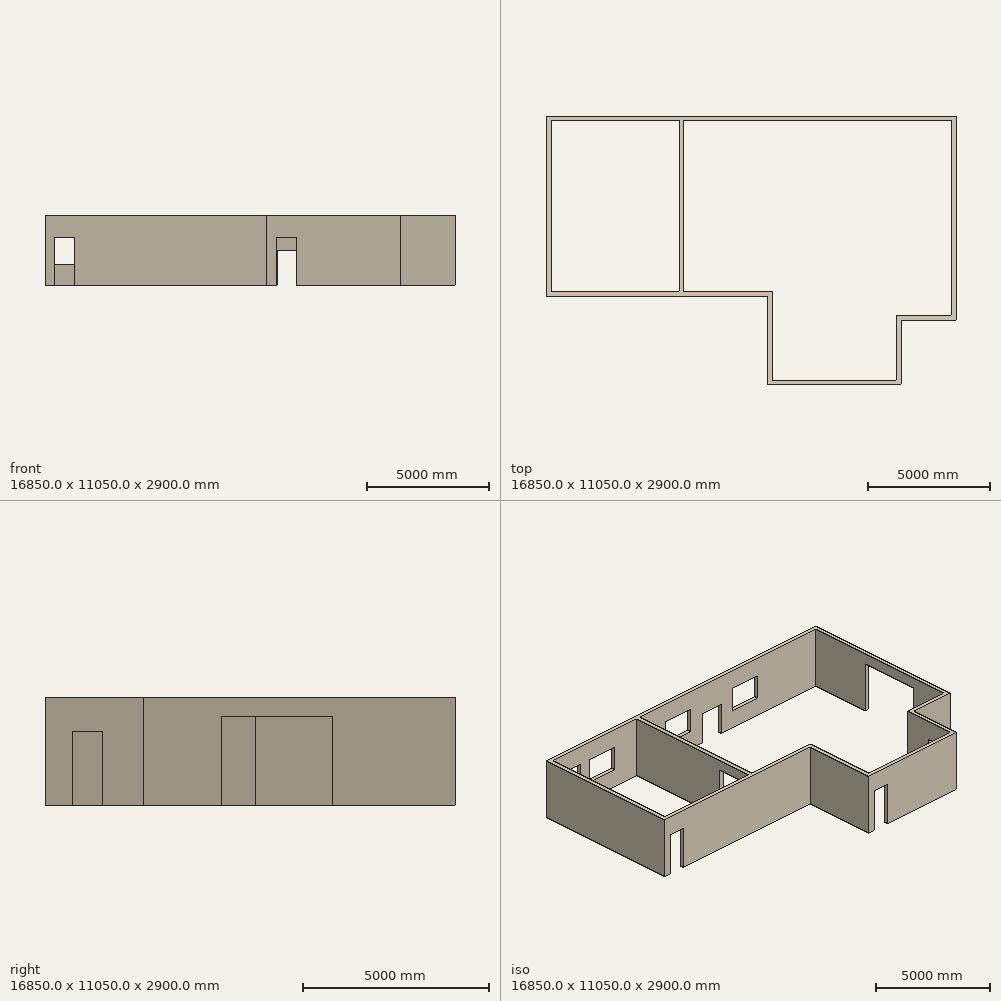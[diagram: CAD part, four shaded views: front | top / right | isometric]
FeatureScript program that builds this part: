
annotation { "Feature Type Name" : "Feature", "Feature Type Description" : "" }
export const myFeature = defineFeature(function(context is Context, id is Id, definition is map)
    precondition{}
    {
        {
            var Q0;
            Q0=qCreatedBy(makeId("Top.planeOp"),FACE);
            var sketch = newSketch(context, id + "F0", { "sketchPlane" : qUnion([Q0])});
            skLineSegment(sketch, "E0", {"start": v(0, 0) * mm, "end": v(0, 7000) * mm});
            skLineSegment(sketch, "E1", {"start": v(0, 7000) * mm, "end": v(5250, 7000) * mm});
            skLineSegment(sketch, "E2", {"start": v(16450, 7000) * mm, "end": v(16450, -1000) * mm});
            skLineSegment(sketch, "E3", {"start": v(16450, -1000) * mm, "end": v(14200, -1000) * mm});
            skLineSegment(sketch, "E4", {"start": v(14200, -1000) * mm, "end": v(14200, -3650) * mm});
            skLineSegment(sketch, "E5", {"start": v(14200, -3650) * mm, "end": v(9100, -3650) * mm});
            skLineSegment(sketch, "E6", {"start": v(9100, -3650) * mm, "end": v(9100, 0) * mm});
            skLineSegment(sketch, "E7", {"start": v(0, 0) * mm, "end": v(5250, 0) * mm});
            skLineSegment(sketch, "E8", {"start": v(5250, 7000) * mm, "end": v(5250, 1800) * mm});
            skLineSegment(sketch, "E9", {"start": v(5250, 1800) * mm, "end": v(5450, 1800) * mm});
            skLineSegment(sketch, "E10", {"start": v(5450, 1800) * mm, "end": v(5450, 7000) * mm});
            skLineSegment(sketch, "E11", {"start": v(5250, 0) * mm, "end": v(5250, 550) * mm});
            skLineSegment(sketch, "E12", {"start": v(5250, 550) * mm, "end": v(5450, 550) * mm});
            skLineSegment(sketch, "E13", {"start": v(5450, 550) * mm, "end": v(5450, 0) * mm});
            skLineSegment(sketch, "E14.0", {"start": v(14400, -1200) * mm, "end": v(14400, -3850) * mm});
            skLineSegment(sketch, "E14.1", {"start": v(16650, -1200) * mm, "end": v(14400, -1200) * mm});
            skLineSegment(sketch, "E14.2", {"start": v(14400, -3850) * mm, "end": v(8900, -3850) * mm});
            skLineSegment(sketch, "E14.3", {"start": v(16650, 7200) * mm, "end": v(16650, -1200) * mm});
            skLineSegment(sketch, "E14.4", {"start": v(8900, -3850) * mm, "end": v(8900, -200) * mm});
            skLineSegment(sketch, "E14.5", {"start": v(-200, -200) * mm, "end": v(8900, -200) * mm});
            skLineSegment(sketch, "E14.6", {"start": v(-200, -200) * mm, "end": v(-200, 7200) * mm});
            skLineSegment(sketch, "E14.7", {"start": v(-200, 7200) * mm, "end": v(16650, 7200) * mm});
            skLineSegment(sketch, "E15.trimOffspring", {"start": v(5450, 7000) * mm, "end": v(16450, 7000) * mm});
            skLineSegment(sketch, "E16.trimOffspring", {"start": v(5450, 0) * mm, "end": v(9100, 0) * mm});
            skSolve(sketch);
        }
        {
            var Q0;
            Q0=makeQuery(id+"F0.imprint","IMPRINT",FACE,{"disambiguationData":[TD([[makeQuery(id+"F0.imprint","IMPRINT",EDGE,{"derivedFrom":sQuery(id+"F0.wireOp",EDGE,"E0")}),1.0]])]});
            extrude(context, id + "F1", {"entities" : qUnion([Q0]), "depth" : 2900 * mm});
        }
        {
            var Q0;
            Q0=makeQuery(id+"F1.opExtrude","SWEPT_FACE",FACE,{"disambiguationData":[OSD([sQuery(id+"F0.wireOp",EDGE,"E14.2")])]});
            var sketch = newSketch(context, id + "F2", { "sketchPlane" : qUnion([Q0])});
            skLineSegment(sketch, "E17.bottom", {"start": v(9300, 0) * mm, "end": v(10100, 0) * mm});
            skLineSegment(sketch, "E17.top", {"start": v(9300, 2000) * mm, "end": v(10100, 2000) * mm});
            skLineSegment(sketch, "E17.left", {"start": v(9300, 0) * mm, "end": v(9300, 2000) * mm});
            skLineSegment(sketch, "E17.right", {"start": v(10100, 0) * mm, "end": v(10100, 2000) * mm});
            skSolve(sketch);
        }
        {
            var Q0;
            Q0 = qSketchRegion(id + "F2", true);
            extrude(context, id + "F3", {"entities" : qUnion([Q0]), "operationType" : NewBodyOperationType.REMOVE, "endBound" : BoundingType.UP_TO_NEXT, "oppositeDirection" : true, "depth" : 25 * mm});
        }
        {
            var Q0;
            Q0=makeQuery(id+"F1.opExtrude","SWEPT_FACE",FACE,{"disambiguationData":[OSD([sQuery(id+"F0.wireOp",EDGE,"E1")])]});
            var sketch = newSketch(context, id + "F4", { "sketchPlane" : qUnion([Q0])});
            skLineSegment(sketch, "E18.bottom", {"start": v(160, 2000) * mm, "end": v(1740, 2000) * mm});
            skLineSegment(sketch, "E18.top", {"start": v(160, 860) * mm, "end": v(1740, 860) * mm});
            skLineSegment(sketch, "E18.left", {"start": v(160, 2000) * mm, "end": v(160, 860) * mm});
            skLineSegment(sketch, "E18.right", {"start": v(1740, 2000) * mm, "end": v(1740, 860) * mm});
            skLineSegment(sketch, "E19.bottom", {"start": v(2300, 2000) * mm, "end": v(3880, 2000) * mm});
            skLineSegment(sketch, "E19.top", {"start": v(2300, 860) * mm, "end": v(3880, 860) * mm});
            skLineSegment(sketch, "E19.left", {"start": v(2300, 2000) * mm, "end": v(2300, 860) * mm});
            skLineSegment(sketch, "E19.right", {"start": v(3880, 2000) * mm, "end": v(3880, 860) * mm});
            skSolve(sketch);
        }
        {
            var Q0;
            Q0 = qSketchRegion(id + "F4", true);
            extrude(context, id + "F5", {"entities" : qUnion([Q0]), "operationType" : NewBodyOperationType.REMOVE, "endBound" : BoundingType.UP_TO_NEXT, "oppositeDirection" : true, "depth" : 25 * mm});
        }
        {
            var Q0;
            Q0=makeQuery(id+"F1.opExtrude","SWEPT_FACE",FACE,{"disambiguationData":[OSD([sQuery(id+"F0.wireOp",EDGE,"E15.trimOffspring")])]});
            var sketch = newSketch(context, id + "F6", { "sketchPlane" : qUnion([Q0])});
            skLineSegment(sketch, "E20.bottom", {"start": v(7050, 2000) * mm, "end": v(8630, 2000) * mm});
            skLineSegment(sketch, "E20.top", {"start": v(7050, 860) * mm, "end": v(8630, 860) * mm});
            skLineSegment(sketch, "E20.left", {"start": v(7050, 2000) * mm, "end": v(7050, 860) * mm});
            skLineSegment(sketch, "E20.right", {"start": v(8630, 2000) * mm, "end": v(8630, 860) * mm});
            skLineSegment(sketch, "E21.bottom", {"start": v(11250, 2000) * mm, "end": v(12830, 2000) * mm});
            skLineSegment(sketch, "E21.top", {"start": v(11250, 860) * mm, "end": v(12830, 860) * mm});
            skLineSegment(sketch, "E21.left", {"start": v(11250, 2000) * mm, "end": v(11250, 860) * mm});
            skLineSegment(sketch, "E21.right", {"start": v(12830, 2000) * mm, "end": v(12830, 860) * mm});
            skLineSegment(sketch, "E22.bottom", {"start": v(9350, 1468.83) * mm, "end": v(10550, 1468.83) * mm});
            skLineSegment(sketch, "E22.top", {"start": v(9350, 0) * mm, "end": v(10550, 0) * mm});
            skLineSegment(sketch, "E22.left", {"start": v(9350, 1468.83) * mm, "end": v(9350, 0) * mm});
            skLineSegment(sketch, "E22.right", {"start": v(10550, 1468.83) * mm, "end": v(10550, 0) * mm});
            skSolve(sketch);
        }
        {
            var Q0;
            Q0=makeQuery(id+"F1.opExtrude","SWEPT_FACE",FACE,{"disambiguationData":[OSD([sQuery(id+"F0.wireOp",EDGE,"E14.3")])]});
            var sketch = newSketch(context, id + "F7", { "sketchPlane" : qUnion([Q0])});
            skLineSegment(sketch, "E23.bottom", {"start": v(884.2, 0) * mm, "end": v(3884.2, 0) * mm});
            skLineSegment(sketch, "E23.top", {"start": v(884.2, 2400) * mm, "end": v(3884.2, 2400) * mm});
            skLineSegment(sketch, "E23.left", {"start": v(884.2, 0) * mm, "end": v(884.2, 2400) * mm});
            skLineSegment(sketch, "E23.right", {"start": v(3884.2, 0) * mm, "end": v(3884.2, 2400) * mm});
            skSolve(sketch);
        }
        {
            var Q0;
            Q0 = qSketchRegion(id + "F7", true);
            extrude(context, id + "F8", {"entities" : qUnion([Q0]), "operationType" : NewBodyOperationType.REMOVE, "endBound" : BoundingType.UP_TO_NEXT, "oppositeDirection" : true, "depth" : 25 * mm});
        }
        {
            var Q0;
            Q0=makeQuery(id+"F1.opExtrude","SWEPT_FACE",FACE,{"disambiguationData":[OSD([sQuery(id+"F0.wireOp",EDGE,"E14.0")])]});
            var sketch = newSketch(context, id + "F9", { "sketchPlane" : qUnion([Q0])});
            skLineSegment(sketch, "E24.bottom", {"start": v(-3122.79, 0) * mm, "end": v(-2322.79, 0) * mm});
            skLineSegment(sketch, "E24.top", {"start": v(-3122.79, 2000) * mm, "end": v(-2322.79, 2000) * mm});
            skLineSegment(sketch, "E24.left", {"start": v(-3122.79, 0) * mm, "end": v(-3122.79, 2000) * mm});
            skLineSegment(sketch, "E24.right", {"start": v(-2322.79, 0) * mm, "end": v(-2322.79, 2000) * mm});
            skSolve(sketch);
        }
        {
            var Q0;
            Q0 = qSketchRegion(id + "F9", true);
            extrude(context, id + "F10", {"entities" : qUnion([Q0]), "operationType" : NewBodyOperationType.REMOVE, "endBound" : BoundingType.UP_TO_NEXT, "oppositeDirection" : true, "depth" : 25 * mm});
        }
        {
            var Q0;
            Q0 = qSketchRegion(id + "F6", true);
            extrude(context, id + "F11", {"entities" : qUnion([Q0]), "operationType" : NewBodyOperationType.REMOVE, "endBound" : BoundingType.UP_TO_NEXT, "oppositeDirection" : true, "depth" : 25 * mm});
        }
        {
            var Q0;
            Q0=makeQuery(id+"F1.opExtrude","SWEPT_FACE",FACE,{"disambiguationData":[OSD([sQuery(id+"F0.wireOp",EDGE,"E10")])]});
            var sketch = newSketch(context, id + "F12", { "sketchPlane" : qUnion([Q0])});
            skLineSegment(sketch, "E25.bottom", {"start": v(1800, 2900) * mm, "end": v(550, 2900) * mm});
            skLineSegment(sketch, "E25.top", {"start": v(1800, 2400) * mm, "end": v(550, 2400) * mm});
            skLineSegment(sketch, "E25.left", {"start": v(1800, 2900) * mm, "end": v(1800, 2400) * mm});
            skLineSegment(sketch, "E25.right", {"start": v(550, 2900) * mm, "end": v(550, 2400) * mm});
            skSolve(sketch);
        }
        {
            var Q0;
            Q0=makeQuery(id+"F12.imprint","IMPRINT",FACE,{"disambiguationData":[TD([[makeQuery(id+"F12.imprint","IMPRINT",EDGE,{"derivedFrom":sQuery(id+"F12.wireOp",EDGE,"E25.bottom")}),1.0]])]});
            extrude(context, id + "F13", {"entities" : qUnion([Q0]), "operationType" : NewBodyOperationType.ADD, "oppositeDirection" : true, "depth" : 200 * mm});
        }
        {
            var Q0;
            Q0=makeQuery(id+"F1.opExtrude","SWEPT_FACE",FACE,{"disambiguationData":[OSD([sQuery(id+"F0.wireOp",EDGE,"E14.5")])]});
            var sketch = newSketch(context, id + "F14", { "sketchPlane" : qUnion([Q0])});
            skLineSegment(sketch, "E26.bottom", {"start": v(180, 0) * mm, "end": v(980, 0) * mm});
            skLineSegment(sketch, "E26.top", {"start": v(180, 2000) * mm, "end": v(980, 2000) * mm});
            skLineSegment(sketch, "E26.left", {"start": v(180, 0) * mm, "end": v(180, 2000) * mm});
            skLineSegment(sketch, "E26.right", {"start": v(980, 0) * mm, "end": v(980, 2000) * mm});
            skSolve(sketch);
        }
        {
            var Q0;
            Q0 = qSketchRegion(id + "F14", true);
            extrude(context, id + "F15", {"entities" : qUnion([Q0]), "operationType" : NewBodyOperationType.REMOVE, "endBound" : BoundingType.UP_TO_NEXT, "oppositeDirection" : true, "depth" : 25 * mm});
        }
    });
